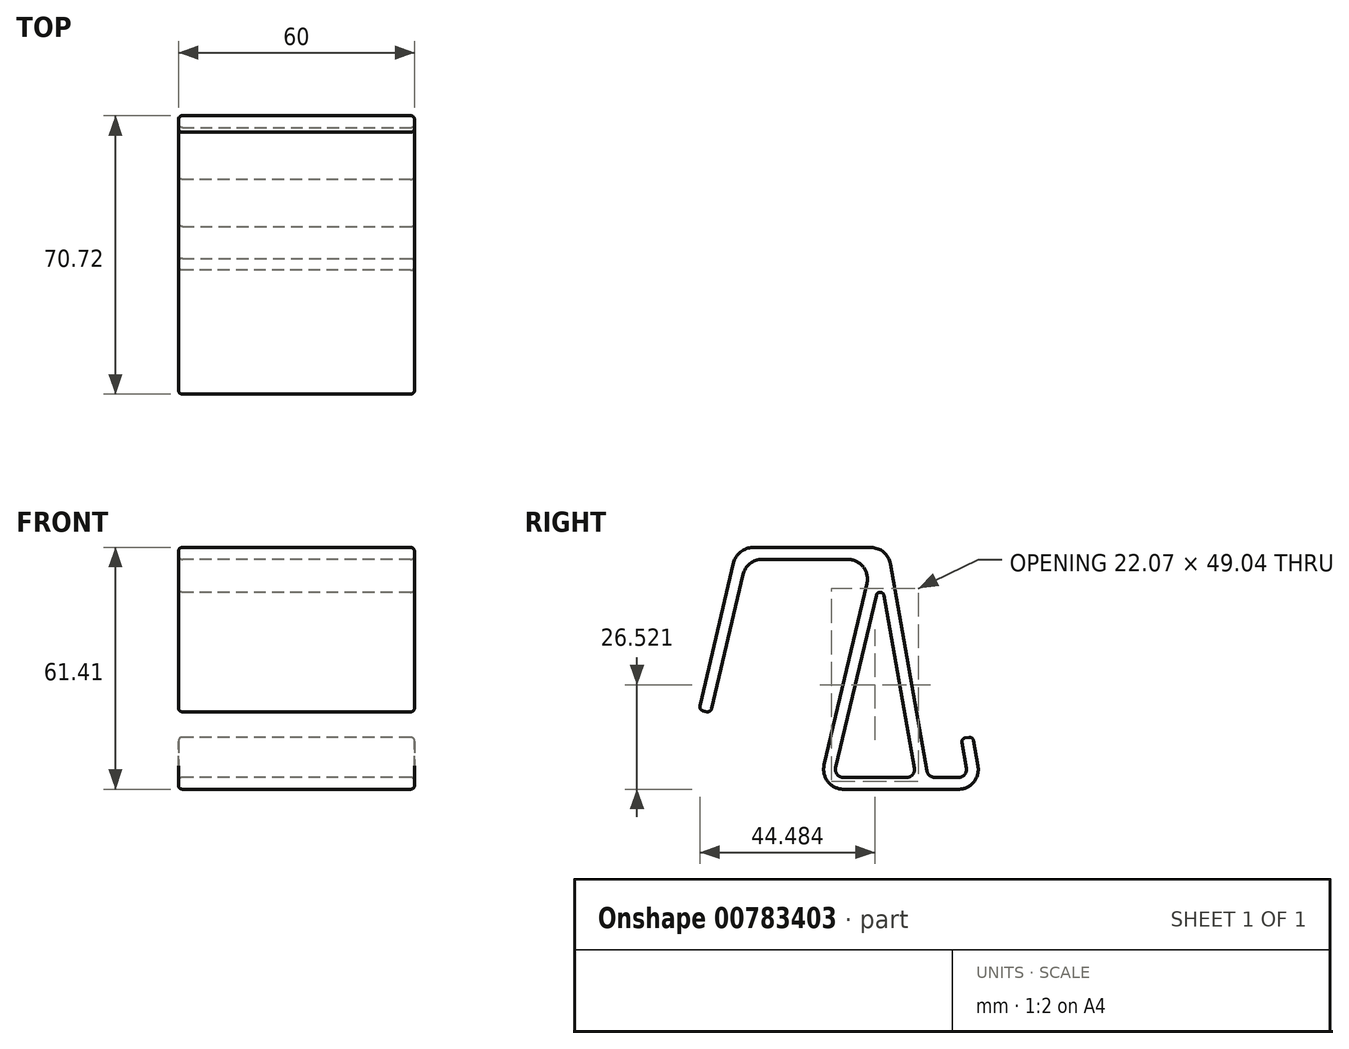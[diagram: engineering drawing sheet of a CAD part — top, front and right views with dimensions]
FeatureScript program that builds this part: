
annotation { "Feature Type Name" : "Feature", "Feature Type Description" : "" }
export const myFeature = defineFeature(function(context is Context, id is Id, definition is map)
    precondition{}
    {
        {
            var Q0;
            Q0=qCreatedBy(makeId("Right.planeOp"),FACE);
            var sketch = newSketch(context, id + "F0", { "sketchPlane" : qUnion([Q0])});
            skLineSegment(sketch, "E0", {"start": v(0, 0) * mm, "end": v(38.16, 0) * mm});
            skLineSegment(sketch, "E1", {"start": v(36.42, -7.4) * mm, "end": v(24.43, -58.4) * mm});
            skLineSegment(sketch, "E2", {"start": v(58.62, -58.4) * mm, "end": v(56.88, -48.56) * mm});
            skLineSegment(sketch, "E3", {"start": v(56.88, -48.56) * mm, "end": v(59.83, -48.04) * mm});
            skLineSegment(sketch, "E4", {"start": v(59.83, -48.04) * mm, "end": v(62.2, -61.4) * mm});
            skLineSegment(sketch, "E5", {"start": v(62.2, -61.4) * mm, "end": v(20.65, -61.4) * mm});
            skLineSegment(sketch, "E6", {"start": v(20.65, -61.4) * mm, "end": v(34.38, -3) * mm});
            skLineSegment(sketch, "E7", {"start": v(34.38, -3) * mm, "end": v(2.38, -3) * mm});
            skLineSegment(sketch, "E8", {"start": v(2.38, -3) * mm, "end": v(-6.78, -41.94) * mm});
            skLineSegment(sketch, "E9", {"start": v(-6.78, -41.94) * mm, "end": v(-9.7, -41.25) * mm});
            skLineSegment(sketch, "E10", {"start": v(-9.7, -41.25) * mm, "end": v(0, 0) * mm});
            skLineSegment(sketch, "E11", {"start": v(38.16, 0) * mm, "end": v(48.46, -58.4) * mm});
            skLineSegment(sketch, "E12.0", {"start": v(36.42, -7.4) * mm, "end": v(45.42, -58.4) * mm});
            skLineSegment(sketch, "E13.trimOffspring", {"start": v(24.43, -58.4) * mm, "end": v(45.42, -58.4) * mm});
            skLineSegment(sketch, "E14.trimOffspring", {"start": v(48.46, -58.4) * mm, "end": v(58.62, -58.4) * mm});
            skSolve(sketch);
        }
        {
            var Q0;
            Q0=makeQuery(id+"F0.imprint","IMPRINT",FACE,{"disambiguationData":[TD([[makeQuery(id+"F0.imprint","IMPRINT",EDGE,{"derivedFrom":sQuery(id+"F0.wireOp",EDGE,"E0")}),-1.0]])]});
            extrude(context, id + "F1", {"entities" : qUnion([Q0]), "depth" : 60 * mm, "offsetDistance" : 25 * mm});
        }
        {
            var Q0;
            Q0=makeQuery(id+"F1.opExtrude","SWEPT_EDGE",EDGE,{"disambiguationData":[OSD([sQuery(id+"F0.wireOp",EDGE,"E0"),sQuery(id+"F0.wireOp",EDGE,"E10")])]});
            var Q1;
            Q1=makeQuery(id+"F1.opExtrude","SWEPT_EDGE",EDGE,{"disambiguationData":[OSD([sQuery(id+"F0.wireOp",EDGE,"E0"),sQuery(id+"F0.wireOp",EDGE,"E11")])]});
            var Q2;
            Q2=makeQuery(id+"F1.opExtrude","SWEPT_EDGE",EDGE,{"disambiguationData":[OSD([sQuery(id+"F0.wireOp",EDGE,"E4"),sQuery(id+"F0.wireOp",EDGE,"E5")])]});
            var Q3;
            Q3=makeQuery(id+"F1.opExtrude","SWEPT_EDGE",EDGE,{"disambiguationData":[OSD([sQuery(id+"F0.wireOp",EDGE,"E5"),sQuery(id+"F0.wireOp",EDGE,"E6")])]});
            var Q4;
            Q4=makeQuery(id+"F1.opExtrude","SWEPT_EDGE",EDGE,{"disambiguationData":[OSD([sQuery(id+"F0.wireOp",EDGE,"E7"),sQuery(id+"F0.wireOp",EDGE,"E8")])]});
            var Q5;
            Q5=makeQuery(id+"F1.opExtrude","SWEPT_EDGE",EDGE,{"disambiguationData":[OSD([sQuery(id+"F0.wireOp",EDGE,"E6"),sQuery(id+"F0.wireOp",EDGE,"E7")])]});
            fillet(context, id + "F2", {"entities" : qUnion([Q0, Q1, Q2, Q3, Q4, Q5]), "radius" : 5 * mm, "tangentPropagation" : true, "allowEdgeOverflow" : false});
        }
        {
            var Q0;
            Q0=makeQuery(id+"F1.opExtrude","CAP_EDGE",EDGE,{"disambiguationData":[OSD([sQuery(id+"F0.wireOp",EDGE,"E0")])],"isStart":false});
            var Q1;
            Q1=makeQuery(id+"F1.opExtrude","CAP_EDGE",EDGE,{"disambiguationData":[OSD([sQuery(id+"F0.wireOp",EDGE,"E11")])],"isStart":true});
            var Q2;
            Q2=makeQuery(id+"F1.opExtrude","CAP_EDGE",EDGE,{"disambiguationData":[OSD([sQuery(id+"F0.wireOp",EDGE,"E7")])],"isStart":false});
            var Q3;
            Q3=makeQuery(id+"F1.opExtrude","CAP_EDGE",EDGE,{"disambiguationData":[OSD([sQuery(id+"F0.wireOp",EDGE,"E6")])],"isStart":true});
            fillet(context, id + "F3", {"entities" : qUnion([Q0, Q1, Q2, Q3]), "radius" : 1 * mm, "tangentPropagation" : true, "allowEdgeOverflow" : false});
        }
        {
            var Q0;
            Q0=makeQuery(id+"F1.opExtrude","SWEPT_EDGE",EDGE,{"disambiguationData":[OSD([sQuery(id+"F0.wireOp",EDGE,"E9"),sQuery(id+"F0.wireOp",EDGE,"E10")])]});
            var Q1;
            Q1=makeQuery(id+"F1.opExtrude","SWEPT_EDGE",EDGE,{"disambiguationData":[OSD([sQuery(id+"F0.wireOp",EDGE,"E8"),sQuery(id+"F0.wireOp",EDGE,"E9")])]});
            var Q2;
            Q2=makeQuery(id+"F1.opExtrude","CAP_EDGE",EDGE,{"disambiguationData":[OSD([sQuery(id+"F0.wireOp",EDGE,"E9")])],"isStart":true});
            var Q3;
            Q3=makeQuery(id+"F1.opExtrude","CAP_EDGE",EDGE,{"disambiguationData":[OSD([sQuery(id+"F0.wireOp",EDGE,"E9")])],"isStart":false});
            fillet(context, id + "F4", {"entities" : qUnion([Q0, Q1, Q2, Q3]), "radius" : 1 * mm, "allowEdgeOverflow" : false});
        }
        {
            var Q0;
            Q0=makeQuery(id+"F1.opExtrude","SWEPT_EDGE",EDGE,{"disambiguationData":[OSD([sQuery(id+"F0.wireOp",EDGE,"E11"),sQuery(id+"F0.wireOp",EDGE,"E14.trimOffspring")])]});
            var Q1;
            Q1=makeQuery(id+"F1.opExtrude","SWEPT_EDGE",EDGE,{"disambiguationData":[OSD([sQuery(id+"F0.wireOp",EDGE,"E2"),sQuery(id+"F0.wireOp",EDGE,"E14.trimOffspring")])]});
            var Q2;
            Q2=makeQuery(id+"F1.opExtrude","SWEPT_EDGE",EDGE,{"disambiguationData":[OSD([sQuery(id+"F0.wireOp",EDGE,"E1"),sQuery(id+"F0.wireOp",EDGE,"E13.trimOffspring")])]});
            var Q3;
            Q3=makeQuery(id+"F1.opExtrude","SWEPT_EDGE",EDGE,{"disambiguationData":[OSD([sQuery(id+"F0.wireOp",EDGE,"E12.0"),sQuery(id+"F0.wireOp",EDGE,"E13.trimOffspring")])]});
            fillet(context, id + "F5", {"entities" : qUnion([Q0, Q1, Q2, Q3]), "radius" : 2 * mm, "tangentPropagation" : true, "allowEdgeOverflow" : false});
        }
        {
            var Q0;
            Q0=makeQuery(id+"F1.opExtrude","SWEPT_EDGE",EDGE,{"disambiguationData":[OSD([sQuery(id+"F0.wireOp",EDGE,"E1"),sQuery(id+"F0.wireOp",EDGE,"E12.0")])]});
            fillet(context, id + "F6", {"entities" : qUnion([Q0]), "radius" : 1 * mm, "tangentPropagation" : true, "allowEdgeOverflow" : false});
        }
        {
            var Q0;
            Q0=makeQuery(id+"F1.opExtrude","CAP_EDGE",EDGE,{"disambiguationData":[OSD([sQuery(id+"F0.wireOp",EDGE,"E1")])],"isStart":false});
            var Q1;
            Q1=makeQuery(id+"F1.opExtrude","CAP_EDGE",EDGE,{"disambiguationData":[OSD([sQuery(id+"F0.wireOp",EDGE,"E12.0")])],"isStart":true});
            var Q2;
            Q2=makeQuery(id+"F1.opExtrude","SWEPT_FACE",FACE,{"disambiguationData":[OSD([sQuery(id+"F0.wireOp",EDGE,"E3")])]});
            var Q3;
            Q3=makeQuery(id+"F1.opExtrude","CAP_EDGE",EDGE,{"disambiguationData":[OSD([sQuery(id+"F0.wireOp",EDGE,"E14.trimOffspring")])],"isStart":true});
            var Q4;
            Q4=makeQuery(id+"F1.opExtrude","CAP_EDGE",EDGE,{"disambiguationData":[OSD([sQuery(id+"F0.wireOp",EDGE,"E2")])],"isStart":false});
            fillet(context, id + "F7", {"entities" : qUnion([Q0, Q1, Q2, Q3, Q4]), "radius" : 1 * mm, "tangentPropagation" : true, "allowEdgeOverflow" : false});
        }
    });
